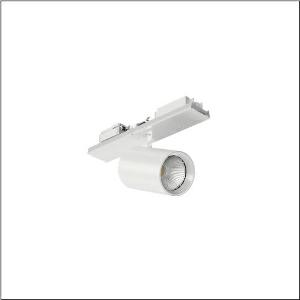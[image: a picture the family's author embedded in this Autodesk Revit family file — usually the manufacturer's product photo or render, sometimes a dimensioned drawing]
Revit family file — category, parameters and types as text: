
# Revit family: licross_r__spot_31_51sl147a45b_9b2d
name_source: partatom
category: Lighting Fixtures
units: mm (PartAtom-declared; Revit-internal decimal feet)

## family parameters
Cut with Voids When Loaded = No
Host = Face
Light Source = No
Part Type = Normal
Room Calculation Point = No
Round Connector Dimension = Use Diameter
Shared = No

## types (1)
- --- (1 x LED, 5250 lm, 42.4 W, 4000K)
    Apparent Load = 42 VA
    CIE Flux Codes = 93 97 100 100 100
    Color Rendering = 90
    Color Temperature = 4000K
    Default Elevation = 1800 mm
    Description = Licross® Spot 31, directional spotlight, light control with lens, of plastic, LED rated luminous flux: 5.250lm, light colour: 940, with plug, 3-pole, with phase selection, mains connection: 220..240V, AC, 50/60Hz, of aluminium, traffic white (RAL 9016), length: 140mm, diameter: 90mm, protection rating (complete): IP20, insulation class (complete): insulation class I (protective earthing), certification: CE, packaging unit: 1 piece
    Height = 175 mm
    Lamp = 1 x LED
    Lamp Light Flux = 5250 lm
    Lamp Power = 42.4 W
    Lamp count = 1
    Length = 90 mm
    Luminous efficacy = 124 lm/W
    Manufacturer = Siteco
    ModVariant = No
    Model = 51SL147A45B
    Mounting Place = Ceiling
    Mounting Type = Pendant
    Number of Poles = 1
    OnlyDefault = Yes
    Power Factor = 1
    Product Name = Licross® Spot 31
    Product group = directional spotlight
    ProductGroupID = 905
    Protection Class = Protection class I
    Protection Degree = IP 20
    RLX_Detail_Level = 1
    RLX_Emergency_Light_Flux = 0 lm
    RLX_Emergency_Type = 0
    RLX_Emergency_Type_DB = No
    RlxData = <blob elided: 14809 chars, md5=aad53753>
    Socket = socket
    Standby Power = 0 W
    System Light Flux = 5250 lm
    System Power = 42 W
    Type Comments = factory setting: luminous flux: 100 % | (ON | ON | ON) | 1050 mA
    Type Image = l_1245720.jpg
    URL = http://relux.com
    VarID = @adj_081731
    Voltage = 0 V
    Weight = 0.00 kg
    Width = 0 mm  [stored 0 ft]

note: [stored X ft] marks values corroborated as IEEE doubles in the binary element streams (Revit-internal decimal feet)

## geometry (parser evidence)
native form markers: Sweep x11
no freeform markers — native parametric forms only
